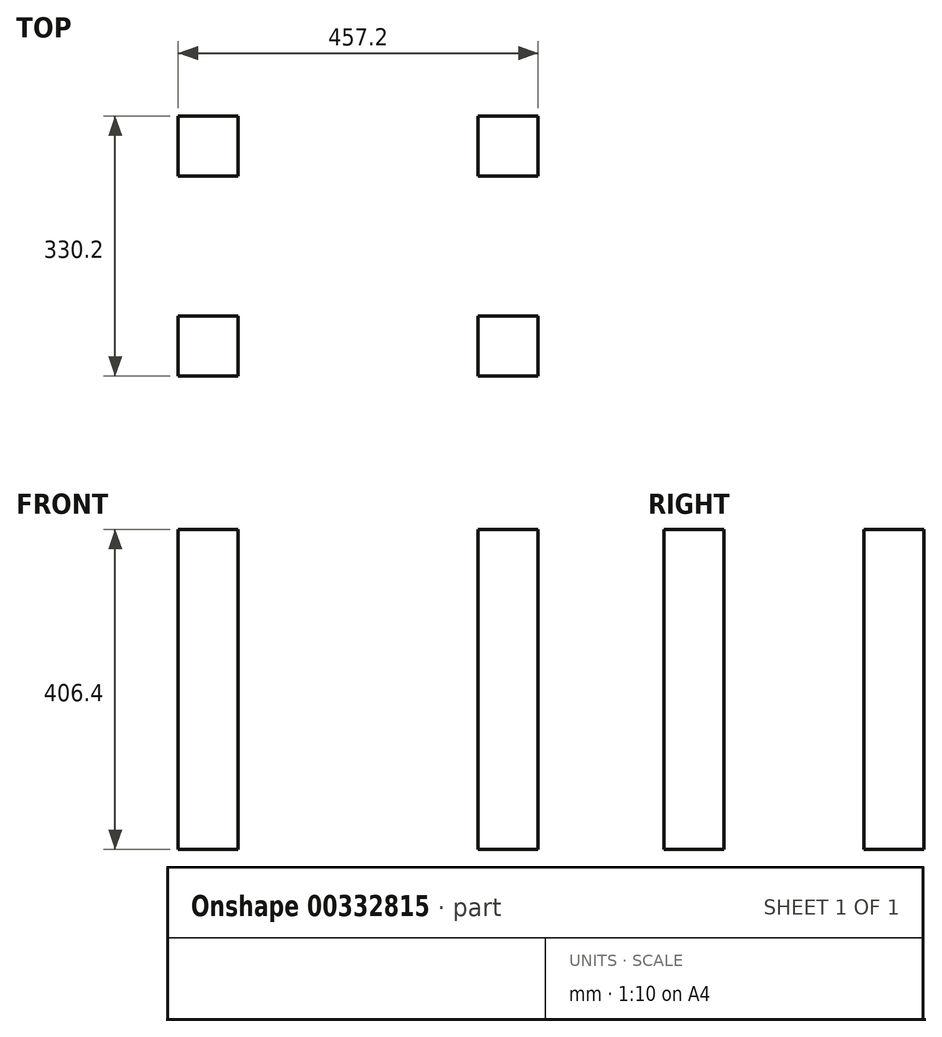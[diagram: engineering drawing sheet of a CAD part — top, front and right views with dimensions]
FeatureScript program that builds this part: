
annotation { "Feature Type Name" : "Feature", "Feature Type Description" : "" }
export const myFeature = defineFeature(function(context is Context, id is Id, definition is map)
    precondition{}
    {
        {
            var Q0;
            Q0=qCreatedBy(makeId("Top.planeOp"),FACE);
            var sketch = newSketch(context, id + "F0", { "sketchPlane" : qUnion([Q0])});
            skLineSegment(sketch, "E0.bottom", {"start": v(-185.34, 127.37) * mm, "end": v(195.66, 127.37) * mm});
            skLineSegment(sketch, "E0.top", {"start": v(-185.34, -126.63) * mm, "end": v(195.66, -126.63) * mm});
            skLineSegment(sketch, "E0.left", {"start": v(-185.34, 127.37) * mm, "end": v(-185.34, -126.63) * mm});
            skLineSegment(sketch, "E0.right", {"start": v(195.66, 127.37) * mm, "end": v(195.66, -126.63) * mm});
            skLineSegment(sketch, "E1.bottom", {"start": v(-147.24, 89.27) * mm, "end": v(-223.44, 89.27) * mm});
            skLineSegment(sketch, "E1.top", {"start": v(-147.24, 165.47) * mm, "end": v(-223.44, 165.47) * mm});
            skLineSegment(sketch, "E1.left", {"start": v(-147.24, 89.27) * mm, "end": v(-147.24, 165.47) * mm});
            skLineSegment(sketch, "E1.right", {"start": v(-223.44, 89.27) * mm, "end": v(-223.44, 165.47) * mm});
            skPoint(sketch, "E1.middle", {"position": v(-185.34, 127.37) * mm});
            skLineSegment(sketch, "E2.bottom", {"start": v(-147.24, -164.73) * mm, "end": v(-223.44, -164.73) * mm});
            skLineSegment(sketch, "E2.top", {"start": v(-147.24, -88.53) * mm, "end": v(-223.44, -88.53) * mm});
            skLineSegment(sketch, "E2.left", {"start": v(-147.24, -164.73) * mm, "end": v(-147.24, -88.53) * mm});
            skLineSegment(sketch, "E2.right", {"start": v(-223.44, -164.73) * mm, "end": v(-223.44, -88.53) * mm});
            skPoint(sketch, "E2.middle", {"position": v(-185.34, -126.63) * mm});
            skPoint(sketch, "E3.middle", {"position": v(150.4, -189.32) * mm});
            skLineSegment(sketch, "E4.bottom", {"start": v(233.76, -164.73) * mm, "end": v(157.56, -164.73) * mm});
            skLineSegment(sketch, "E4.top", {"start": v(233.76, -88.53) * mm, "end": v(157.56, -88.53) * mm});
            skLineSegment(sketch, "E4.left", {"start": v(233.76, -164.73) * mm, "end": v(233.76, -88.53) * mm});
            skLineSegment(sketch, "E4.right", {"start": v(157.56, -164.73) * mm, "end": v(157.56, -88.53) * mm});
            skPoint(sketch, "E4.middle", {"position": v(195.66, -126.63) * mm});
            skLineSegment(sketch, "E5.bottom", {"start": v(233.76, 89.27) * mm, "end": v(157.56, 89.27) * mm});
            skLineSegment(sketch, "E5.top", {"start": v(233.76, 165.47) * mm, "end": v(157.56, 165.47) * mm});
            skLineSegment(sketch, "E5.left", {"start": v(233.76, 89.27) * mm, "end": v(233.76, 165.47) * mm});
            skLineSegment(sketch, "E5.right", {"start": v(157.56, 89.27) * mm, "end": v(157.56, 165.47) * mm});
            skPoint(sketch, "E5.middle", {"position": v(195.66, 127.37) * mm});
            skSolve(sketch);
        }
        {
            var Q0;
            {var subQ4=sQuery(id+"F0.wireOp",EDGE,"E2.bottom");Q0=makeQuery(id+"F0.imprint","IMPRINT",FACE,{"disambiguationData":[TD([[makeQuery(id+"F0.imprint","IMPRINT",EDGE,{"derivedFrom":subQ4}),-1.0]])]});}
            var Q1;
            {var subQ0=sQuery(id+"F0.wireOp",EDGE,"E0.left");var subQ1=sQuery(id+"F0.wireOp",EDGE,"E0.top");var subQ2=makeQuery(id+"F0.imprint","INTERSECT",VERTEX,{"derivedFrom":[subQ1,subQ0]});Q1=makeQuery(id+"F0.imprint","IMPRINT",FACE,{"disambiguationData":[TD([[makeQuery(id+"F0.imprint","IMPRINT",EDGE,{"disambiguationData":[TD([[subQ2,-1.0]])],"derivedFrom":subQ1}),1.0]])]});}
            var Q2;
            {var subQ0=sQuery(id+"F0.wireOp",EDGE,"E0.right");var subQ1=sQuery(id+"F0.wireOp",EDGE,"E0.top");var subQ2=makeQuery(id+"F0.imprint","INTERSECT",VERTEX,{"derivedFrom":[subQ1,subQ0]});Q2=makeQuery(id+"F0.imprint","IMPRINT",FACE,{"disambiguationData":[TD([[makeQuery(id+"F0.imprint","IMPRINT",EDGE,{"disambiguationData":[TD([[subQ2,1.0]])],"derivedFrom":subQ1}),1.0]])]});}
            var Q3;
            {var subQ0=sQuery(id+"F0.wireOp",EDGE,"E4.bottom");Q3=makeQuery(id+"F0.imprint","IMPRINT",FACE,{"disambiguationData":[TD([[makeQuery(id+"F0.imprint","IMPRINT",EDGE,{"derivedFrom":subQ0}),-1.0]])]});}
            var Q4;
            {var subQ0=sQuery(id+"F0.wireOp",EDGE,"E0.right");var subQ1=sQuery(id+"F0.wireOp",EDGE,"E0.bottom");var subQ2=makeQuery(id+"F0.imprint","INTERSECT",VERTEX,{"derivedFrom":[subQ1,subQ0]});Q4=makeQuery(id+"F0.imprint","IMPRINT",FACE,{"disambiguationData":[TD([[makeQuery(id+"F0.imprint","IMPRINT",EDGE,{"disambiguationData":[TD([[subQ2,1.0]])],"derivedFrom":subQ1}),-1.0]])]});}
            var Q5;
            {var subQ6=sQuery(id+"F0.wireOp",EDGE,"E5.top");Q5=makeQuery(id+"F0.imprint","IMPRINT",FACE,{"disambiguationData":[TD([[makeQuery(id+"F0.imprint","IMPRINT",EDGE,{"derivedFrom":subQ6}),1.0]])]});}
            var Q6;
            {var subQ0=sQuery(id+"F0.wireOp",EDGE,"E0.left");var subQ1=sQuery(id+"F0.wireOp",EDGE,"E0.bottom");var subQ2=makeQuery(id+"F0.imprint","INTERSECT",VERTEX,{"derivedFrom":[subQ1,subQ0]});Q6=makeQuery(id+"F0.imprint","IMPRINT",FACE,{"disambiguationData":[TD([[makeQuery(id+"F0.imprint","IMPRINT",EDGE,{"disambiguationData":[TD([[subQ2,-1.0]])],"derivedFrom":subQ1}),-1.0]])]});}
            var Q7;
            {var subQ0=sQuery(id+"F0.wireOp",EDGE,"E1.top");Q7=makeQuery(id+"F0.imprint","IMPRINT",FACE,{"disambiguationData":[TD([[makeQuery(id+"F0.imprint","IMPRINT",EDGE,{"derivedFrom":subQ0}),1.0]])]});}
            extrude(context, id + "F1", {"entities" : qUnion([Q0, Q1, Q2, Q3, Q4, Q5, Q6, Q7]), "oppositeDirection" : true, "depth" : 406.4 * mm});
        }
    });
